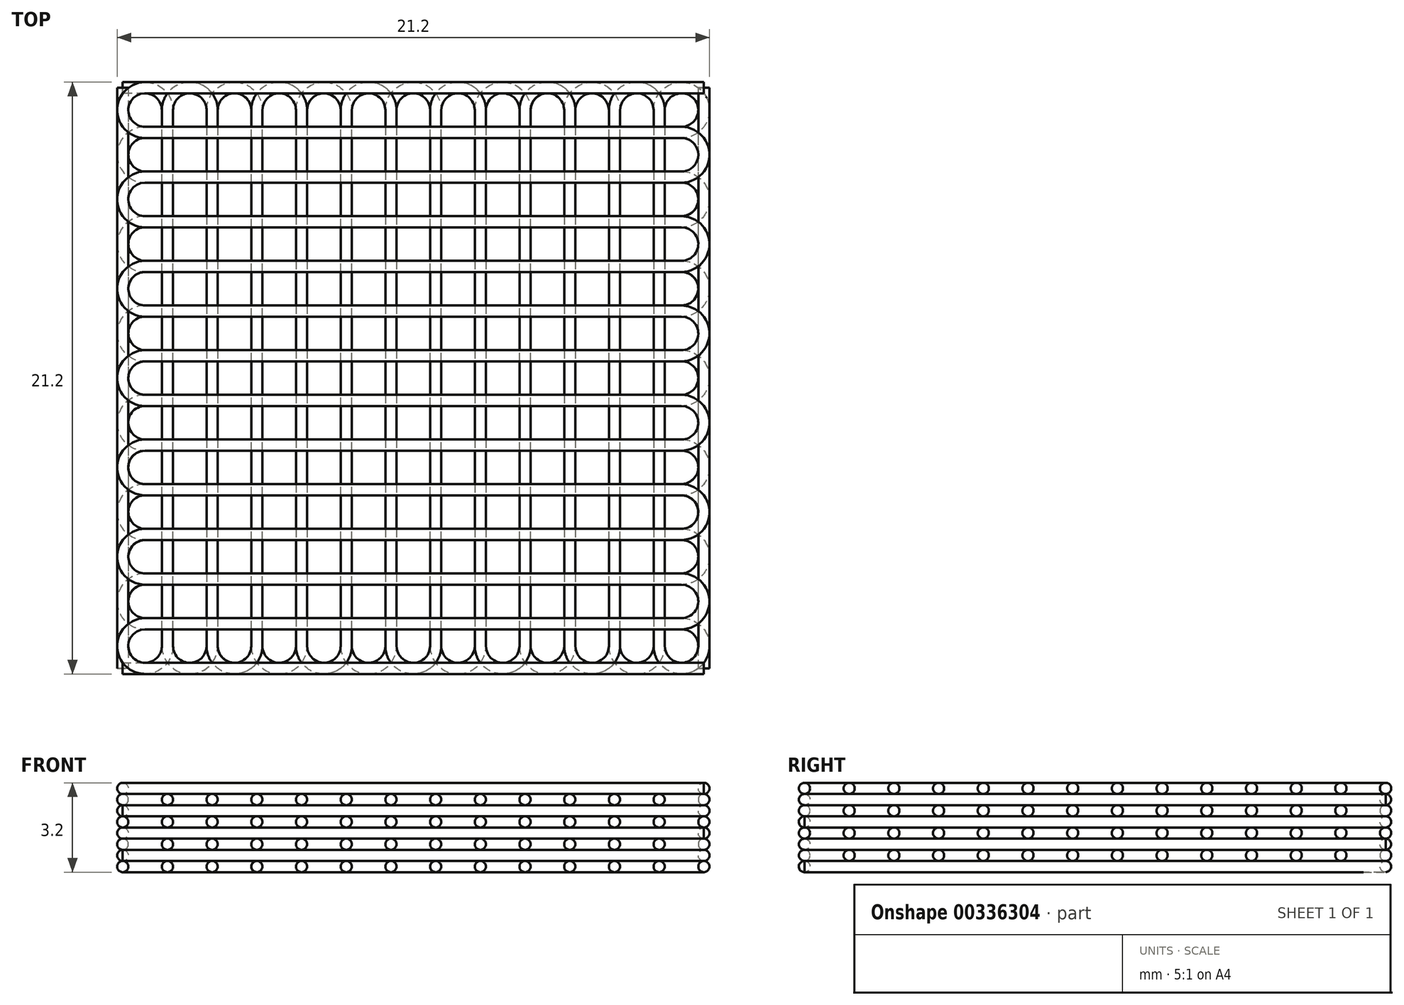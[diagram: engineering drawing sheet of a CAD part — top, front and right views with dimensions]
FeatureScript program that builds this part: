
annotation { "Feature Type Name" : "Feature", "Feature Type Description" : "" }
export const myFeature = defineFeature(function(context is Context, id is Id, definition is map)
    precondition{}
    {
        {
            var Q0;
            Q0=qCreatedBy(makeId("Top.planeOp"),FACE);
            cPlane(context, id + "F0", {"entities" : qUnion([Q0]), "cplaneType" : CPlaneType.OFFSET, "offset" : 0.2 * mm, "width" : 150 * mm, "height" : 150 * mm});
        }
        {
            var Q0;
            Q0=qCreatedBy(id+"F0.planeOp",FACE);
            var sketch = newSketch(context, id + "F1", { "sketchPlane" : qUnion([Q0])});
            skLineSegment(sketch, "E0.bottom", {"start": v(10.4, 10.4) * mm, "end": v(-10.4, 10.4) * mm});
            skLineSegment(sketch, "E0.top", {"start": v(10.4, -10.4) * mm, "end": v(-10.4, -10.4) * mm});
            skLineSegment(sketch, "E0.left", {"start": v(10.4, 9.6) * mm, "end": v(10.4, -10.4) * mm});
            skLineSegment(sketch, "E0.right", {"start": v(-10.4, 10.4) * mm, "end": v(-10.4, -10.4) * mm});
            skPoint(sketch, "E0.middle", {"position": v(0, 0) * mm});
            skLineSegment(sketch, "E1", {"start": v(7.2, 10.4) * mm, "end": v(7.2, -9.6) * mm});
            skLineSegment(sketch, "E2", {"start": v(8.8, -9.6) * mm, "end": v(8.8, 9.6) * mm});
            skLineSegment(sketch, "E3", {"start": v(10.4, 10.4) * mm, "end": v(10.4, -10.4) * mm});
            skArc(sketch, "E4", {"start": v(8.8, 9.6) * mm, "mid": v(9.6, 10.4) * mm, "end": v(10.4, 9.6) * mm});
            skArc(sketch, "E5", {"start": v(8.8, -9.6) * mm, "mid": v(8, -10.4) * mm, "end": v(7.2, -9.6) * mm});
            skLineSegment(sketch, "E6", {"start": v(7.2, -9.6) * mm, "end": v(7.2, 9.6) * mm});
            skLineSegment(sketch, "E7", {"start": v(10.4, 9.6) * mm, "end": v(10.4, -9.6) * mm});
            skLineSegment(sketch, "E8.1.0.0", {"start": v(7.2, 9.6) * mm, "end": v(7.2, -9.6) * mm});
            skArc(sketch, "E8.1.0.1", {"start": v(5.6, 9.6) * mm, "mid": v(6.4, 10.4) * mm, "end": v(7.2, 9.6) * mm});
            skLineSegment(sketch, "E8.1.0.2", {"start": v(5.6, -9.6) * mm, "end": v(5.6, 9.6) * mm});
            skArc(sketch, "E8.1.0.3", {"start": v(5.6, -9.6) * mm, "mid": v(4.8, -10.4) * mm, "end": v(4, -9.6) * mm});
            skLineSegment(sketch, "E8.1.0.4", {"start": v(4, -9.6) * mm, "end": v(4, 9.6) * mm});
            skLineSegment(sketch, "E8.2.0.0", {"start": v(4, 9.6) * mm, "end": v(4, -9.6) * mm});
            skArc(sketch, "E8.2.0.1", {"start": v(2.4, 9.6) * mm, "mid": v(3.2, 10.4) * mm, "end": v(4, 9.6) * mm});
            skLineSegment(sketch, "E8.2.0.2", {"start": v(2.4, -9.6) * mm, "end": v(2.4, 9.6) * mm});
            skArc(sketch, "E8.2.0.3", {"start": v(2.4, -9.6) * mm, "mid": v(1.6, -10.4) * mm, "end": v(0.8, -9.6) * mm});
            skLineSegment(sketch, "E8.2.0.4", {"start": v(0.8, -9.6) * mm, "end": v(0.8, 9.6) * mm});
            skLineSegment(sketch, "E8.3.0.0", {"start": v(0.8, 9.6) * mm, "end": v(0.8, -9.6) * mm});
            skArc(sketch, "E8.3.0.1", {"start": v(-0.8, 9.6) * mm, "mid": v(0, 10.4) * mm, "end": v(0.8, 9.6) * mm});
            skLineSegment(sketch, "E8.3.0.2", {"start": v(-0.8, -9.6) * mm, "end": v(-0.8, 9.6) * mm});
            skArc(sketch, "E8.3.0.3", {"start": v(-0.8, -9.6) * mm, "mid": v(-1.6, -10.4) * mm, "end": v(-2.4, -9.6) * mm});
            skLineSegment(sketch, "E8.3.0.4", {"start": v(-2.4, -9.6) * mm, "end": v(-2.4, 9.6) * mm});
            skLineSegment(sketch, "E8.4.0.0", {"start": v(-2.4, 9.6) * mm, "end": v(-2.4, -9.6) * mm});
            skArc(sketch, "E8.4.0.1", {"start": v(-4, 9.6) * mm, "mid": v(-3.2, 10.4) * mm, "end": v(-2.4, 9.6) * mm});
            skLineSegment(sketch, "E8.4.0.2", {"start": v(-4, -9.6) * mm, "end": v(-4, 9.6) * mm});
            skArc(sketch, "E8.4.0.3", {"start": v(-4, -9.6) * mm, "mid": v(-4.8, -10.4) * mm, "end": v(-5.6, -9.6) * mm});
            skLineSegment(sketch, "E8.4.0.4", {"start": v(-5.6, -9.6) * mm, "end": v(-5.6, 9.6) * mm});
            skLineSegment(sketch, "E8.5.0.0", {"start": v(-5.6, 9.6) * mm, "end": v(-5.6, -9.6) * mm});
            skArc(sketch, "E8.5.0.1", {"start": v(-7.2, 9.6) * mm, "mid": v(-6.4, 10.4) * mm, "end": v(-5.6, 9.6) * mm});
            skLineSegment(sketch, "E8.5.0.2", {"start": v(-7.2, -9.6) * mm, "end": v(-7.2, 9.6) * mm});
            skArc(sketch, "E8.5.0.3", {"start": v(-7.2, -9.6) * mm, "mid": v(-8, -10.4) * mm, "end": v(-8.8, -9.6) * mm});
            skLineSegment(sketch, "E8.5.0.4", {"start": v(-8.8, -9.6) * mm, "end": v(-8.8, 9.6) * mm});
            skLineSegment(sketch, "E8.direction1", {"start": v(7.2, -9.6) * mm, "end": v(4, -9.6) * mm, "construction": true});
            skArc(sketch, "E9", {"start": v(-8.8, 9.6) * mm, "mid": v(-9.6, 10.4) * mm, "end": v(-10.4, 9.6) * mm});
            skLineSegment(sketch, "E10", {"start": v(-10.4, 9.6) * mm, "end": v(-10.4, -10.4) * mm});
            skSolve(sketch);
        }
        {
            var Q0;
            Q0=sQuery(id+"F1.wireOp",EDGE,"E3");
            var Q1;
            Q1=sQuery(id+"F1.wireOp",VERTEX,"E0.left.end");
            cPlane(context, id + "F2", {"entities" : qUnion([Q0, Q1]), "cplaneType" : CPlaneType.LINE_POINT, "offset" : 25 * mm, "width" : 150 * mm, "height" : 150 * mm});
        }
        {
            var Q0;
            Q0=qCreatedBy(id+"F2.planeOp",FACE);
            var sketch = newSketch(context, id + "F3", { "sketchPlane" : qUnion([Q0])});
            skCircle(sketch, "E11", {"center": v(10.4, 0.2) * mm, "radius": 0.2 * mm});
            skSolve(sketch);
        }
        {
            var Q0;
            Q0=makeQuery(id+"F3.imprint","IMPRINT",FACE,{"disambiguationData":[TD([[makeQuery(id+"F3.imprint","IMPRINT",EDGE,{"derivedFrom":sQuery(id+"F3.wireOp",EDGE,"E11")}),1.0]])]});
            var Q1;
            Q1=sQuery(id+"F1.wireOp",EDGE,"E4");
            var Q2;
            Q2=sQuery(id+"F1.wireOp",EDGE,"E2");
            var Q3;
            Q3=sQuery(id+"F1.wireOp",EDGE,"E0.left");
            var Q4;
            Q4=sQuery(id+"F1.wireOp",EDGE,"E5");
            var Q5;
            Q5=sQuery(id+"F1.wireOp",EDGE,"E8.1.0.1");
            var Q6;
            Q6=sQuery(id+"F1.wireOp",EDGE,"E8.1.0.2");
            var Q7;
            Q7=sQuery(id+"F1.wireOp",EDGE,"E8.1.0.0");
            var Q8;
            Q8=sQuery(id+"F1.wireOp",EDGE,"E8.1.0.3");
            var Q9;
            Q9=sQuery(id+"F1.wireOp",EDGE,"E8.2.0.0");
            var Q10;
            Q10=sQuery(id+"F1.wireOp",EDGE,"E8.2.0.1");
            var Q11;
            Q11=sQuery(id+"F1.wireOp",EDGE,"E8.2.0.2");
            var Q12;
            Q12=sQuery(id+"F1.wireOp",EDGE,"E8.3.0.0");
            var Q13;
            Q13=sQuery(id+"F1.wireOp",EDGE,"E8.3.0.1");
            var Q14;
            Q14=sQuery(id+"F1.wireOp",EDGE,"E8.3.0.2");
            var Q15;
            Q15=sQuery(id+"F1.wireOp",EDGE,"E8.4.0.1");
            var Q16;
            Q16=sQuery(id+"F1.wireOp",EDGE,"E8.3.0.4");
            var Q17;
            Q17=sQuery(id+"F1.wireOp",EDGE,"E8.4.0.2");
            var Q18;
            Q18=sQuery(id+"F1.wireOp",EDGE,"E8.5.0.0");
            var Q19;
            Q19=sQuery(id+"F1.wireOp",EDGE,"E8.5.0.1");
            var Q20;
            Q20=sQuery(id+"F1.wireOp",EDGE,"E8.5.0.2");
            var Q21;
            Q21=sQuery(id+"F1.wireOp",EDGE,"E8.5.0.4");
            var Q22;
            Q22=sQuery(id+"F1.wireOp",EDGE,"E9");
            var Q23;
            Q23=sQuery(id+"F1.wireOp",EDGE,"E8.2.0.3");
            var Q24;
            Q24=sQuery(id+"F1.wireOp",EDGE,"E8.3.0.3");
            var Q25;
            Q25=sQuery(id+"F1.wireOp",EDGE,"E8.4.0.3");
            var Q26;
            Q26=sQuery(id+"F1.wireOp",EDGE,"E8.5.0.3");
            var Q27;
            Q27=sQuery(id+"F1.wireOp",EDGE,"E10");
            sweep(context, id + "F4", {"profiles" : qUnion([Q0]), "path" : qUnion([Q1, Q2, Q3, Q4, Q5, Q6, Q7, Q8, Q9, Q10, Q11, Q12, Q13, Q14, Q15, Q16, Q17, Q18, Q19, Q20, Q21, Q22, Q23, Q24, Q25, Q26, Q27])});
        }
        {
            var Q0;
            Q0=qCreatedBy(id+"F0.planeOp",FACE);
            cPlane(context, id + "F5", {"entities" : qUnion([Q0]), "cplaneType" : CPlaneType.OFFSET, "offset" : 0.4 * mm, "width" : 150 * mm, "height" : 150 * mm});
        }
        {
            var Q0;
            Q0=qCreatedBy(id+"F5.planeOp",FACE);
            var sketch = newSketch(context, id + "F6", { "sketchPlane" : qUnion([Q0])});
            skLineSegment(sketch, "E12.bottom", {"start": v(10.4, -10.4) * mm, "end": v(10.4, 10.4) * mm});
            skLineSegment(sketch, "E12.top", {"start": v(-10.4, -10.4) * mm, "end": v(-10.4, 10.4) * mm});
            skLineSegment(sketch, "E12.left", {"start": v(9.6, -10.4) * mm, "end": v(-10.4, -10.4) * mm});
            skLineSegment(sketch, "E12.right", {"start": v(10.4, 10.4) * mm, "end": v(-10.4, 10.4) * mm});
            skPoint(sketch, "E12.middle", {"position": v(0, 0) * mm});
            skLineSegment(sketch, "E13", {"start": v(10.4, -7.2) * mm, "end": v(-9.6, -7.2) * mm});
            skLineSegment(sketch, "E14", {"start": v(-9.6, -8.8) * mm, "end": v(9.6, -8.8) * mm});
            skLineSegment(sketch, "E15", {"start": v(10.4, -10.4) * mm, "end": v(-10.4, -10.4) * mm});
            skArc(sketch, "E16", {"start": v(9.6, -8.8) * mm, "mid": v(10.4, -9.6) * mm, "end": v(9.6, -10.4) * mm});
            skArc(sketch, "E17", {"start": v(-9.6, -8.8) * mm, "mid": v(-10.4, -8) * mm, "end": v(-9.6, -7.2) * mm});
            skLineSegment(sketch, "E18", {"start": v(-9.6, -7.2) * mm, "end": v(9.6, -7.2) * mm});
            skLineSegment(sketch, "E19", {"start": v(9.6, -10.4) * mm, "end": v(-9.6, -10.4) * mm});
            skLineSegment(sketch, "E20.1.0.0", {"start": v(9.6, -7.2) * mm, "end": v(-9.6, -7.2) * mm});
            skArc(sketch, "E20.1.0.1", {"start": v(9.6, -5.6) * mm, "mid": v(10.4, -6.4) * mm, "end": v(9.6, -7.2) * mm});
            skLineSegment(sketch, "E20.1.0.2", {"start": v(-9.6, -5.6) * mm, "end": v(9.6, -5.6) * mm});
            skArc(sketch, "E20.1.0.3", {"start": v(-9.6, -5.6) * mm, "mid": v(-10.4, -4.8) * mm, "end": v(-9.6, -4) * mm});
            skLineSegment(sketch, "E20.1.0.4", {"start": v(-9.6, -4) * mm, "end": v(9.6, -4) * mm});
            skLineSegment(sketch, "E20.2.0.0", {"start": v(9.6, -4) * mm, "end": v(-9.6, -4) * mm});
            skArc(sketch, "E20.2.0.1", {"start": v(9.6, -2.4) * mm, "mid": v(10.4, -3.2) * mm, "end": v(9.6, -4) * mm});
            skLineSegment(sketch, "E20.2.0.2", {"start": v(-9.6, -2.4) * mm, "end": v(9.6, -2.4) * mm});
            skArc(sketch, "E20.2.0.3", {"start": v(-9.6, -2.4) * mm, "mid": v(-10.4, -1.6) * mm, "end": v(-9.6, -0.8) * mm});
            skLineSegment(sketch, "E20.2.0.4", {"start": v(-9.6, -0.8) * mm, "end": v(9.6, -0.8) * mm});
            skLineSegment(sketch, "E20.3.0.0", {"start": v(9.6, -0.8) * mm, "end": v(-9.6, -0.8) * mm});
            skArc(sketch, "E20.3.0.1", {"start": v(9.6, 0.8) * mm, "mid": v(10.4, 0) * mm, "end": v(9.6, -0.8) * mm});
            skLineSegment(sketch, "E20.3.0.2", {"start": v(-9.6, 0.8) * mm, "end": v(9.6, 0.8) * mm});
            skArc(sketch, "E20.3.0.3", {"start": v(-9.6, 0.8) * mm, "mid": v(-10.4, 1.6) * mm, "end": v(-9.6, 2.4) * mm});
            skLineSegment(sketch, "E20.3.0.4", {"start": v(-9.6, 2.4) * mm, "end": v(9.6, 2.4) * mm});
            skLineSegment(sketch, "E20.4.0.0", {"start": v(9.6, 2.4) * mm, "end": v(-9.6, 2.4) * mm});
            skArc(sketch, "E20.4.0.1", {"start": v(9.6, 4) * mm, "mid": v(10.4, 3.2) * mm, "end": v(9.6, 2.4) * mm});
            skLineSegment(sketch, "E20.4.0.2", {"start": v(-9.6, 4) * mm, "end": v(9.6, 4) * mm});
            skArc(sketch, "E20.4.0.3", {"start": v(-9.6, 4) * mm, "mid": v(-10.4, 4.8) * mm, "end": v(-9.6, 5.6) * mm});
            skLineSegment(sketch, "E20.4.0.4", {"start": v(-9.6, 5.6) * mm, "end": v(9.6, 5.6) * mm});
            skLineSegment(sketch, "E20.5.0.0", {"start": v(9.6, 5.6) * mm, "end": v(-9.6, 5.6) * mm});
            skArc(sketch, "E20.5.0.1", {"start": v(9.6, 7.2) * mm, "mid": v(10.4, 6.4) * mm, "end": v(9.6, 5.6) * mm});
            skLineSegment(sketch, "E20.5.0.2", {"start": v(-9.6, 7.2) * mm, "end": v(9.6, 7.2) * mm});
            skArc(sketch, "E20.5.0.3", {"start": v(-9.6, 7.2) * mm, "mid": v(-10.4, 8) * mm, "end": v(-9.6, 8.8) * mm});
            skLineSegment(sketch, "E20.5.0.4", {"start": v(-9.6, 8.8) * mm, "end": v(9.6, 8.8) * mm});
            skLineSegment(sketch, "E20.direction1", {"start": v(-9.6, -7.2) * mm, "end": v(-9.6, -4) * mm, "construction": true});
            skArc(sketch, "E21", {"start": v(9.6, 8.8) * mm, "mid": v(10.4, 9.6) * mm, "end": v(9.6, 10.4) * mm});
            skLineSegment(sketch, "E22", {"start": v(9.6, 10.4) * mm, "end": v(-10.4, 10.4) * mm});
            skSolve(sketch);
        }
        {
            var Q0;
            Q0=sQuery(id+"F6.wireOp",EDGE,"E15");
            var Q1;
            Q1=sQuery(id+"F6.wireOp",VERTEX,"E12.left.end");
            cPlane(context, id + "F7", {"entities" : qUnion([Q0, Q1]), "cplaneType" : CPlaneType.LINE_POINT, "offset" : 25 * mm, "width" : 150 * mm, "height" : 150 * mm});
        }
        {
            var Q0;
            Q0=qCreatedBy(id+"F7.planeOp",FACE);
            var sketch = newSketch(context, id + "F8", { "sketchPlane" : qUnion([Q0])});
            skCircle(sketch, "E23", {"center": v(10.4, 0.6) * mm, "radius": 0.2 * mm});
            skSolve(sketch);
        }
        {
            var Q0;
            Q0=makeQuery(id+"F8.imprint","IMPRINT",FACE,{"disambiguationData":[TD([[makeQuery(id+"F8.imprint","IMPRINT",EDGE,{"derivedFrom":sQuery(id+"F8.wireOp",EDGE,"E23")}),1.0]])]});
            var Q1;
            Q1=sQuery(id+"F6.wireOp",EDGE,"E12.left");
            var Q2;
            Q2=sQuery(id+"F6.wireOp",EDGE,"E16");
            var Q3;
            Q3=sQuery(id+"F6.wireOp",EDGE,"E14");
            var Q4;
            Q4=sQuery(id+"F6.wireOp",EDGE,"E17");
            var Q5;
            Q5=sQuery(id+"F6.wireOp",EDGE,"E20.1.0.0");
            var Q6;
            Q6=sQuery(id+"F6.wireOp",EDGE,"E20.1.0.1");
            var Q7;
            Q7=sQuery(id+"F6.wireOp",EDGE,"E20.1.0.2");
            var Q8;
            Q8=sQuery(id+"F6.wireOp",EDGE,"E20.1.0.3");
            var Q9;
            Q9=sQuery(id+"F6.wireOp",EDGE,"E20.1.0.4");
            var Q10;
            Q10=sQuery(id+"F6.wireOp",EDGE,"E20.2.0.1");
            var Q11;
            Q11=sQuery(id+"F6.wireOp",EDGE,"E20.2.0.2");
            var Q12;
            Q12=sQuery(id+"F6.wireOp",EDGE,"E20.2.0.3");
            var Q13;
            Q13=sQuery(id+"F6.wireOp",EDGE,"E20.3.0.0");
            var Q14;
            Q14=sQuery(id+"F6.wireOp",EDGE,"E20.3.0.1");
            var Q15;
            Q15=sQuery(id+"F6.wireOp",EDGE,"E20.3.0.2");
            var Q16;
            Q16=sQuery(id+"F6.wireOp",EDGE,"E20.3.0.3");
            var Q17;
            Q17=sQuery(id+"F6.wireOp",EDGE,"E20.3.0.4");
            var Q18;
            Q18=sQuery(id+"F6.wireOp",EDGE,"E20.4.0.2");
            var Q19;
            Q19=sQuery(id+"F6.wireOp",EDGE,"E20.4.0.3");
            var Q20;
            Q20=sQuery(id+"F6.wireOp",EDGE,"E20.5.0.0");
            var Q21;
            Q21=sQuery(id+"F6.wireOp",EDGE,"E20.5.0.2");
            var Q22;
            Q22=sQuery(id+"F6.wireOp",EDGE,"E20.5.0.3");
            var Q23;
            Q23=sQuery(id+"F6.wireOp",EDGE,"E20.5.0.4");
            var Q24;
            Q24=sQuery(id+"F6.wireOp",EDGE,"E22");
            var Q25;
            Q25=sQuery(id+"F6.wireOp",EDGE,"E21");
            var Q26;
            Q26=sQuery(id+"F6.wireOp",EDGE,"E20.5.0.1");
            var Q27;
            Q27=sQuery(id+"F6.wireOp",EDGE,"E20.4.0.1");
            sweep(context, id + "F9", {"operationType" : NewBodyOperationType.ADD, "profiles" : qUnion([Q0]), "path" : qUnion([Q1, Q2, Q3, Q4, Q5, Q6, Q7, Q8, Q9, Q10, Q11, Q12, Q13, Q14, Q15, Q16, Q17, Q18, Q19, Q20, Q21, Q22, Q23, Q24, Q25, Q26, Q27])});
        }
        {
            var Q0;
            Q0=qCreatedBy(id+"F5.planeOp",FACE);
            cPlane(context, id + "F10", {"entities" : qUnion([Q0]), "cplaneType" : CPlaneType.OFFSET, "offset" : 0.4 * mm, "width" : 150 * mm, "height" : 150 * mm});
        }
        {
            var Q0;
            Q0=qCreatedBy(id+"F10.planeOp",FACE);
            var sketch = newSketch(context, id + "F11", { "sketchPlane" : qUnion([Q0])});
            skLineSegment(sketch, "E24.bottom", {"start": v(-10.4, -10.4) * mm, "end": v(10.4, -10.4) * mm});
            skLineSegment(sketch, "E24.top", {"start": v(-10.4, 10.4) * mm, "end": v(10.4, 10.4) * mm});
            skLineSegment(sketch, "E24.left", {"start": v(-10.4, -9.6) * mm, "end": v(-10.4, 10.4) * mm});
            skLineSegment(sketch, "E24.right", {"start": v(10.4, -10.4) * mm, "end": v(10.4, 10.4) * mm});
            skPoint(sketch, "E24.middle", {"position": v(0, 0) * mm});
            skLineSegment(sketch, "E25", {"start": v(-7.2, -10.4) * mm, "end": v(-7.2, 9.6) * mm});
            skLineSegment(sketch, "E26", {"start": v(-8.8, 9.6) * mm, "end": v(-8.8, -9.6) * mm});
            skLineSegment(sketch, "E27", {"start": v(-10.4, -10.4) * mm, "end": v(-10.4, 10.4) * mm});
            skArc(sketch, "E28", {"start": v(-8.8, -9.6) * mm, "mid": v(-9.6, -10.4) * mm, "end": v(-10.4, -9.6) * mm});
            skArc(sketch, "E29", {"start": v(-8.8, 9.6) * mm, "mid": v(-8, 10.4) * mm, "end": v(-7.2, 9.6) * mm});
            skLineSegment(sketch, "E30", {"start": v(-7.2, 9.6) * mm, "end": v(-7.2, -9.6) * mm});
            skLineSegment(sketch, "E31", {"start": v(-10.4, -9.6) * mm, "end": v(-10.4, 9.6) * mm});
            skLineSegment(sketch, "E32.1.0.0", {"start": v(-7.2, -9.6) * mm, "end": v(-7.2, 9.6) * mm});
            skArc(sketch, "E32.1.0.1", {"start": v(-5.6, -9.6) * mm, "mid": v(-6.4, -10.4) * mm, "end": v(-7.2, -9.6) * mm});
            skLineSegment(sketch, "E32.1.0.2", {"start": v(-5.6, 9.6) * mm, "end": v(-5.6, -9.6) * mm});
            skArc(sketch, "E32.1.0.3", {"start": v(-5.6, 9.6) * mm, "mid": v(-4.8, 10.4) * mm, "end": v(-4, 9.6) * mm});
            skLineSegment(sketch, "E32.1.0.4", {"start": v(-4, 9.6) * mm, "end": v(-4, -9.6) * mm});
            skLineSegment(sketch, "E32.2.0.0", {"start": v(-4, -9.6) * mm, "end": v(-4, 9.6) * mm});
            skArc(sketch, "E32.2.0.1", {"start": v(-2.4, -9.6) * mm, "mid": v(-3.2, -10.4) * mm, "end": v(-4, -9.6) * mm});
            skLineSegment(sketch, "E32.2.0.2", {"start": v(-2.4, 9.6) * mm, "end": v(-2.4, -9.6) * mm});
            skArc(sketch, "E32.2.0.3", {"start": v(-2.4, 9.6) * mm, "mid": v(-1.6, 10.4) * mm, "end": v(-0.8, 9.6) * mm});
            skLineSegment(sketch, "E32.2.0.4", {"start": v(-0.8, 9.6) * mm, "end": v(-0.8, -9.6) * mm});
            skLineSegment(sketch, "E32.3.0.0", {"start": v(-0.8, -9.6) * mm, "end": v(-0.8, 9.6) * mm});
            skArc(sketch, "E32.3.0.1", {"start": v(0.8, -9.6) * mm, "mid": v(0, -10.4) * mm, "end": v(-0.8, -9.6) * mm});
            skLineSegment(sketch, "E32.3.0.2", {"start": v(0.8, 9.6) * mm, "end": v(0.8, -9.6) * mm});
            skArc(sketch, "E32.3.0.3", {"start": v(0.8, 9.6) * mm, "mid": v(1.6, 10.4) * mm, "end": v(2.4, 9.6) * mm});
            skLineSegment(sketch, "E32.3.0.4", {"start": v(2.4, 9.6) * mm, "end": v(2.4, -9.6) * mm});
            skLineSegment(sketch, "E32.4.0.0", {"start": v(2.4, -9.6) * mm, "end": v(2.4, 9.6) * mm});
            skArc(sketch, "E32.4.0.1", {"start": v(4, -9.6) * mm, "mid": v(3.2, -10.4) * mm, "end": v(2.4, -9.6) * mm});
            skLineSegment(sketch, "E32.4.0.2", {"start": v(4, 9.6) * mm, "end": v(4, -9.6) * mm});
            skArc(sketch, "E32.4.0.3", {"start": v(4, 9.6) * mm, "mid": v(4.8, 10.4) * mm, "end": v(5.6, 9.6) * mm});
            skLineSegment(sketch, "E32.4.0.4", {"start": v(5.6, 9.6) * mm, "end": v(5.6, -9.6) * mm});
            skLineSegment(sketch, "E32.5.0.0", {"start": v(5.6, -9.6) * mm, "end": v(5.6, 9.6) * mm});
            skArc(sketch, "E32.5.0.1", {"start": v(7.2, -9.6) * mm, "mid": v(6.4, -10.4) * mm, "end": v(5.6, -9.6) * mm});
            skLineSegment(sketch, "E32.5.0.2", {"start": v(7.2, 9.6) * mm, "end": v(7.2, -9.6) * mm});
            skArc(sketch, "E32.5.0.3", {"start": v(7.2, 9.6) * mm, "mid": v(8, 10.4) * mm, "end": v(8.8, 9.6) * mm});
            skLineSegment(sketch, "E32.5.0.4", {"start": v(8.8, 9.6) * mm, "end": v(8.8, -9.6) * mm});
            skLineSegment(sketch, "E32.direction1", {"start": v(-7.2, 9.6) * mm, "end": v(-4, 9.6) * mm, "construction": true});
            skArc(sketch, "E33", {"start": v(8.8, -9.6) * mm, "mid": v(9.6, -10.4) * mm, "end": v(10.4, -9.6) * mm});
            skLineSegment(sketch, "E34", {"start": v(10.4, -9.6) * mm, "end": v(10.4, 10.4) * mm});
            skSolve(sketch);
        }
        {
            var Q0;
            Q0=sQuery(id+"F11.wireOp",EDGE,"E27");
            var Q1;
            Q1=sQuery(id+"F11.wireOp",VERTEX,"E24.left.end");
            cPlane(context, id + "F12", {"entities" : qUnion([Q0, Q1]), "cplaneType" : CPlaneType.LINE_POINT, "offset" : 25 * mm, "width" : 150 * mm, "height" : 150 * mm});
        }
        {
            var Q0;
            Q0=qCreatedBy(id+"F12.planeOp",FACE);
            var sketch = newSketch(context, id + "F13", { "sketchPlane" : qUnion([Q0])});
            skCircle(sketch, "E35", {"center": v(10.4, 1) * mm, "radius": 0.2 * mm});
            skSolve(sketch);
        }
        {
            var Q0;
            Q0=makeQuery(id+"F13.imprint","IMPRINT",FACE,{"disambiguationData":[TD([[makeQuery(id+"F13.imprint","IMPRINT",EDGE,{"derivedFrom":sQuery(id+"F13.wireOp",EDGE,"E35")}),1.0]])]});
            var Q1;
            Q1=sQuery(id+"F11.wireOp",EDGE,"E24.left");
            var Q2;
            Q2=sQuery(id+"F11.wireOp",EDGE,"E28");
            var Q3;
            Q3=sQuery(id+"F11.wireOp",EDGE,"E26");
            var Q4;
            Q4=sQuery(id+"F11.wireOp",EDGE,"E29");
            var Q5;
            Q5=sQuery(id+"F11.wireOp",EDGE,"E32.1.0.0");
            var Q6;
            Q6=sQuery(id+"F11.wireOp",EDGE,"E32.1.0.1");
            var Q7;
            Q7=sQuery(id+"F11.wireOp",EDGE,"E32.1.0.2");
            var Q8;
            Q8=sQuery(id+"F11.wireOp",EDGE,"E32.1.0.3");
            var Q9;
            Q9=sQuery(id+"F11.wireOp",EDGE,"E32.2.0.0");
            var Q10;
            Q10=sQuery(id+"F11.wireOp",EDGE,"E32.2.0.1");
            var Q11;
            Q11=sQuery(id+"F11.wireOp",EDGE,"E32.2.0.2");
            var Q12;
            Q12=sQuery(id+"F11.wireOp",EDGE,"E32.2.0.3");
            var Q13;
            Q13=sQuery(id+"F11.wireOp",EDGE,"E32.3.0.0");
            var Q14;
            Q14=sQuery(id+"F11.wireOp",EDGE,"E32.3.0.1");
            var Q15;
            Q15=sQuery(id+"F11.wireOp",EDGE,"E32.3.0.2");
            var Q16;
            Q16=sQuery(id+"F11.wireOp",EDGE,"E32.3.0.3");
            var Q17;
            Q17=sQuery(id+"F11.wireOp",EDGE,"E32.3.0.4");
            var Q18;
            Q18=sQuery(id+"F11.wireOp",EDGE,"E32.4.0.1");
            var Q19;
            Q19=sQuery(id+"F11.wireOp",EDGE,"E32.4.0.2");
            var Q20;
            Q20=sQuery(id+"F11.wireOp",EDGE,"E32.4.0.3");
            var Q21;
            Q21=sQuery(id+"F11.wireOp",EDGE,"E32.5.0.0");
            var Q22;
            Q22=sQuery(id+"F11.wireOp",EDGE,"E32.5.0.1");
            var Q23;
            Q23=sQuery(id+"F11.wireOp",EDGE,"E32.5.0.2");
            var Q24;
            Q24=sQuery(id+"F11.wireOp",EDGE,"E32.5.0.3");
            var Q25;
            Q25=sQuery(id+"F11.wireOp",EDGE,"E32.5.0.4");
            var Q26;
            Q26=sQuery(id+"F11.wireOp",EDGE,"E33");
            var Q27;
            Q27=sQuery(id+"F11.wireOp",EDGE,"E34");
            sweep(context, id + "F14", {"operationType" : NewBodyOperationType.ADD, "profiles" : qUnion([Q0]), "path" : qUnion([Q1, Q2, Q3, Q4, Q5, Q6, Q7, Q8, Q9, Q10, Q11, Q12, Q13, Q14, Q15, Q16, Q17, Q18, Q19, Q20, Q21, Q22, Q23, Q24, Q25, Q26, Q27])});
        }
        {
            var Q0;
            Q0=qCreatedBy(id+"F10.planeOp",FACE);
            cPlane(context, id + "F15", {"entities" : qUnion([Q0]), "cplaneType" : CPlaneType.OFFSET, "offset" : 0.4 * mm, "width" : 150 * mm, "height" : 150 * mm});
        }
        {
            var Q0;
            Q0=qCreatedBy(id+"F15.planeOp",FACE);
            var sketch = newSketch(context, id + "F16", { "sketchPlane" : qUnion([Q0])});
            skLineSegment(sketch, "E36.bottom", {"start": v(-10.4, 10.4) * mm, "end": v(-10.4, -10.4) * mm});
            skLineSegment(sketch, "E36.top", {"start": v(10.4, 10.4) * mm, "end": v(10.4, -10.4) * mm});
            skLineSegment(sketch, "E36.left", {"start": v(-9.6, 10.4) * mm, "end": v(10.4, 10.4) * mm});
            skLineSegment(sketch, "E36.right", {"start": v(-10.4, -10.4) * mm, "end": v(10.4, -10.4) * mm});
            skPoint(sketch, "E36.middle", {"position": v(0, 0) * mm});
            skLineSegment(sketch, "E37", {"start": v(-10.4, 7.2) * mm, "end": v(9.6, 7.2) * mm});
            skLineSegment(sketch, "E38", {"start": v(9.6, 8.8) * mm, "end": v(-9.6, 8.8) * mm});
            skLineSegment(sketch, "E39", {"start": v(-10.4, 10.4) * mm, "end": v(10.4, 10.4) * mm});
            skArc(sketch, "E40", {"start": v(-9.6, 8.8) * mm, "mid": v(-10.4, 9.6) * mm, "end": v(-9.6, 10.4) * mm});
            skArc(sketch, "E41", {"start": v(9.6, 8.8) * mm, "mid": v(10.4, 8) * mm, "end": v(9.6, 7.2) * mm});
            skLineSegment(sketch, "E42", {"start": v(9.6, 7.2) * mm, "end": v(-9.6, 7.2) * mm});
            skLineSegment(sketch, "E43", {"start": v(-9.6, 10.4) * mm, "end": v(9.6, 10.4) * mm});
            skLineSegment(sketch, "E44.1.0.0", {"start": v(-9.6, 7.2) * mm, "end": v(9.6, 7.2) * mm});
            skArc(sketch, "E44.1.0.1", {"start": v(-9.6, 5.6) * mm, "mid": v(-10.4, 6.4) * mm, "end": v(-9.6, 7.2) * mm});
            skLineSegment(sketch, "E44.1.0.2", {"start": v(9.6, 5.6) * mm, "end": v(-9.6, 5.6) * mm});
            skArc(sketch, "E44.1.0.3", {"start": v(9.6, 5.6) * mm, "mid": v(10.4, 4.8) * mm, "end": v(9.6, 4) * mm});
            skLineSegment(sketch, "E44.1.0.4", {"start": v(9.6, 4) * mm, "end": v(-9.6, 4) * mm});
            skLineSegment(sketch, "E44.2.0.0", {"start": v(-9.6, 4) * mm, "end": v(9.6, 4) * mm});
            skArc(sketch, "E44.2.0.1", {"start": v(-9.6, 2.4) * mm, "mid": v(-10.4, 3.2) * mm, "end": v(-9.6, 4) * mm});
            skLineSegment(sketch, "E44.2.0.2", {"start": v(9.6, 2.4) * mm, "end": v(-9.6, 2.4) * mm});
            skArc(sketch, "E44.2.0.3", {"start": v(9.6, 2.4) * mm, "mid": v(10.4, 1.6) * mm, "end": v(9.6, 0.8) * mm});
            skLineSegment(sketch, "E44.2.0.4", {"start": v(9.6, 0.8) * mm, "end": v(-9.6, 0.8) * mm});
            skLineSegment(sketch, "E44.3.0.0", {"start": v(-9.6, 0.8) * mm, "end": v(9.6, 0.8) * mm});
            skArc(sketch, "E44.3.0.1", {"start": v(-9.6, -0.8) * mm, "mid": v(-10.4, 0) * mm, "end": v(-9.6, 0.8) * mm});
            skLineSegment(sketch, "E44.3.0.2", {"start": v(9.6, -0.8) * mm, "end": v(-9.6, -0.8) * mm});
            skArc(sketch, "E44.3.0.3", {"start": v(9.6, -0.8) * mm, "mid": v(10.4, -1.6) * mm, "end": v(9.6, -2.4) * mm});
            skLineSegment(sketch, "E44.3.0.4", {"start": v(9.6, -2.4) * mm, "end": v(-9.6, -2.4) * mm});
            skLineSegment(sketch, "E44.4.0.0", {"start": v(-9.6, -2.4) * mm, "end": v(9.6, -2.4) * mm});
            skArc(sketch, "E44.4.0.1", {"start": v(-9.6, -4) * mm, "mid": v(-10.4, -3.2) * mm, "end": v(-9.6, -2.4) * mm});
            skLineSegment(sketch, "E44.4.0.2", {"start": v(9.6, -4) * mm, "end": v(-9.6, -4) * mm});
            skArc(sketch, "E44.4.0.3", {"start": v(9.6, -4) * mm, "mid": v(10.4, -4.8) * mm, "end": v(9.6, -5.6) * mm});
            skLineSegment(sketch, "E44.4.0.4", {"start": v(9.6, -5.6) * mm, "end": v(-9.6, -5.6) * mm});
            skLineSegment(sketch, "E44.5.0.0", {"start": v(-9.6, -5.6) * mm, "end": v(9.6, -5.6) * mm});
            skArc(sketch, "E44.5.0.1", {"start": v(-9.6, -7.2) * mm, "mid": v(-10.4, -6.4) * mm, "end": v(-9.6, -5.6) * mm});
            skLineSegment(sketch, "E44.5.0.2", {"start": v(9.6, -7.2) * mm, "end": v(-9.6, -7.2) * mm});
            skArc(sketch, "E44.5.0.3", {"start": v(9.6, -7.2) * mm, "mid": v(10.4, -8) * mm, "end": v(9.6, -8.8) * mm});
            skLineSegment(sketch, "E44.5.0.4", {"start": v(9.6, -8.8) * mm, "end": v(-9.6, -8.8) * mm});
            skLineSegment(sketch, "E44.direction1", {"start": v(9.6, 7.2) * mm, "end": v(9.6, 4) * mm, "construction": true});
            skArc(sketch, "E45", {"start": v(-9.6, -8.8) * mm, "mid": v(-10.4, -9.6) * mm, "end": v(-9.6, -10.4) * mm});
            skLineSegment(sketch, "E46", {"start": v(-9.6, -10.4) * mm, "end": v(10.4, -10.4) * mm});
            skSolve(sketch);
        }
        {
            var Q0;
            Q0=sQuery(id+"F16.wireOp",EDGE,"E39");
            var Q1;
            Q1=sQuery(id+"F16.wireOp",VERTEX,"E36.left.end");
            cPlane(context, id + "F17", {"entities" : qUnion([Q0, Q1]), "cplaneType" : CPlaneType.LINE_POINT, "offset" : 25 * mm, "width" : 150 * mm, "height" : 150 * mm});
        }
        {
            var Q0;
            Q0=qCreatedBy(id+"F17.planeOp",FACE);
            var sketch = newSketch(context, id + "F18", { "sketchPlane" : qUnion([Q0])});
            skCircle(sketch, "E47", {"center": v(10.4, 1.4) * mm, "radius": 0.2 * mm});
            skSolve(sketch);
        }
        {
            var Q0;
            Q0=makeQuery(id+"F18.imprint","IMPRINT",FACE,{"disambiguationData":[TD([[makeQuery(id+"F18.imprint","IMPRINT",EDGE,{"derivedFrom":sQuery(id+"F18.wireOp",EDGE,"E47")}),1.0]])]});
            var Q1;
            Q1=sQuery(id+"F16.wireOp",EDGE,"E36.left");
            var Q2;
            Q2=sQuery(id+"F16.wireOp",EDGE,"E40");
            var Q3;
            Q3=sQuery(id+"F16.wireOp",EDGE,"E38");
            var Q4;
            Q4=sQuery(id+"F16.wireOp",EDGE,"E44.1.0.0");
            var Q5;
            Q5=sQuery(id+"F16.wireOp",EDGE,"E44.1.0.1");
            var Q6;
            Q6=sQuery(id+"F16.wireOp",EDGE,"E44.1.0.2");
            var Q7;
            Q7=sQuery(id+"F16.wireOp",EDGE,"E44.2.0.0");
            var Q8;
            Q8=sQuery(id+"F16.wireOp",EDGE,"E44.2.0.1");
            var Q9;
            Q9=sQuery(id+"F16.wireOp",EDGE,"E44.2.0.2");
            var Q10;
            Q10=sQuery(id+"F16.wireOp",EDGE,"E44.3.0.0");
            var Q11;
            Q11=sQuery(id+"F16.wireOp",EDGE,"E44.3.0.1");
            var Q12;
            Q12=sQuery(id+"F16.wireOp",EDGE,"E44.3.0.2");
            var Q13;
            Q13=sQuery(id+"F16.wireOp",EDGE,"E44.4.0.0");
            var Q14;
            Q14=sQuery(id+"F16.wireOp",EDGE,"E44.4.0.1");
            var Q15;
            Q15=sQuery(id+"F16.wireOp",EDGE,"E44.4.0.2");
            var Q16;
            Q16=sQuery(id+"F16.wireOp",EDGE,"E44.5.0.0");
            var Q17;
            Q17=sQuery(id+"F16.wireOp",EDGE,"E44.5.0.1");
            var Q18;
            Q18=sQuery(id+"F16.wireOp",EDGE,"E44.5.0.2");
            var Q19;
            Q19=sQuery(id+"F16.wireOp",EDGE,"E44.5.0.4");
            var Q20;
            Q20=sQuery(id+"F16.wireOp",EDGE,"E45");
            var Q21;
            Q21=sQuery(id+"F16.wireOp",EDGE,"E44.5.0.3");
            var Q22;
            Q22=sQuery(id+"F16.wireOp",EDGE,"E44.4.0.3");
            var Q23;
            Q23=sQuery(id+"F16.wireOp",EDGE,"E44.3.0.3");
            var Q24;
            Q24=sQuery(id+"F16.wireOp",EDGE,"E44.1.0.3");
            var Q25;
            Q25=sQuery(id+"F16.wireOp",EDGE,"E44.2.0.3");
            var Q26;
            Q26=sQuery(id+"F16.wireOp",EDGE,"E41");
            var Q27;
            Q27=sQuery(id+"F16.wireOp",EDGE,"E46");
            sweep(context, id + "F19", {"operationType" : NewBodyOperationType.ADD, "profiles" : qUnion([Q0]), "path" : qUnion([Q1, Q2, Q3, Q4, Q5, Q6, Q7, Q8, Q9, Q10, Q11, Q12, Q13, Q14, Q15, Q16, Q17, Q18, Q19, Q20, Q21, Q22, Q23, Q24, Q25, Q26, Q27])});
        }
        {
            var Q0;
            Q0=qCreatedBy(id+"F15.planeOp",FACE);
            cPlane(context, id + "F20", {"entities" : qUnion([Q0]), "cplaneType" : CPlaneType.OFFSET, "offset" : 0.4 * mm, "width" : 150 * mm, "height" : 150 * mm});
        }
        {
            var Q0;
            Q0=qCreatedBy(id+"F20.planeOp",FACE);
            var sketch = newSketch(context, id + "F21", { "sketchPlane" : qUnion([Q0])});
            skLineSegment(sketch, "E48.bottom", {"start": v(10.4, 10.4) * mm, "end": v(-10.4, 10.4) * mm});
            skLineSegment(sketch, "E48.top", {"start": v(10.4, -10.4) * mm, "end": v(-10.4, -10.4) * mm});
            skLineSegment(sketch, "E48.left", {"start": v(10.4, 9.6) * mm, "end": v(10.4, -10.4) * mm});
            skLineSegment(sketch, "E48.right", {"start": v(-10.4, 10.4) * mm, "end": v(-10.4, -10.4) * mm});
            skPoint(sketch, "E48.middle", {"position": v(0, 0) * mm});
            skLineSegment(sketch, "E49", {"start": v(7.2, 10.4) * mm, "end": v(7.2, -9.6) * mm});
            skLineSegment(sketch, "E50", {"start": v(8.8, -9.6) * mm, "end": v(8.8, 9.6) * mm});
            skLineSegment(sketch, "E51", {"start": v(10.4, 10.4) * mm, "end": v(10.4, -10.4) * mm});
            skArc(sketch, "E52", {"start": v(8.8, 9.6) * mm, "mid": v(9.6, 10.4) * mm, "end": v(10.4, 9.6) * mm});
            skArc(sketch, "E53", {"start": v(8.8, -9.6) * mm, "mid": v(8, -10.4) * mm, "end": v(7.2, -9.6) * mm});
            skLineSegment(sketch, "E54", {"start": v(7.2, -9.6) * mm, "end": v(7.2, 9.6) * mm});
            skLineSegment(sketch, "E55", {"start": v(10.4, 9.6) * mm, "end": v(10.4, -9.6) * mm});
            skLineSegment(sketch, "E56.1.0.0", {"start": v(7.2, 9.6) * mm, "end": v(7.2, -9.6) * mm});
            skArc(sketch, "E56.1.0.1", {"start": v(5.6, 9.6) * mm, "mid": v(6.4, 10.4) * mm, "end": v(7.2, 9.6) * mm});
            skLineSegment(sketch, "E56.1.0.2", {"start": v(5.6, -9.6) * mm, "end": v(5.6, 9.6) * mm});
            skArc(sketch, "E56.1.0.3", {"start": v(5.6, -9.6) * mm, "mid": v(4.8, -10.4) * mm, "end": v(4, -9.6) * mm});
            skLineSegment(sketch, "E56.1.0.4", {"start": v(4, -9.6) * mm, "end": v(4, 9.6) * mm});
            skLineSegment(sketch, "E56.2.0.0", {"start": v(4, 9.6) * mm, "end": v(4, -9.6) * mm});
            skArc(sketch, "E56.2.0.1", {"start": v(2.4, 9.6) * mm, "mid": v(3.2, 10.4) * mm, "end": v(4, 9.6) * mm});
            skLineSegment(sketch, "E56.2.0.2", {"start": v(2.4, -9.6) * mm, "end": v(2.4, 9.6) * mm});
            skArc(sketch, "E56.2.0.3", {"start": v(2.4, -9.6) * mm, "mid": v(1.6, -10.4) * mm, "end": v(0.8, -9.6) * mm});
            skLineSegment(sketch, "E56.2.0.4", {"start": v(0.8, -9.6) * mm, "end": v(0.8, 9.6) * mm});
            skLineSegment(sketch, "E56.3.0.0", {"start": v(0.8, 9.6) * mm, "end": v(0.8, -9.6) * mm});
            skArc(sketch, "E56.3.0.1", {"start": v(-0.8, 9.6) * mm, "mid": v(0, 10.4) * mm, "end": v(0.8, 9.6) * mm});
            skLineSegment(sketch, "E56.3.0.2", {"start": v(-0.8, -9.6) * mm, "end": v(-0.8, 9.6) * mm});
            skArc(sketch, "E56.3.0.3", {"start": v(-0.8, -9.6) * mm, "mid": v(-1.6, -10.4) * mm, "end": v(-2.4, -9.6) * mm});
            skLineSegment(sketch, "E56.3.0.4", {"start": v(-2.4, -9.6) * mm, "end": v(-2.4, 9.6) * mm});
            skLineSegment(sketch, "E56.4.0.0", {"start": v(-2.4, 9.6) * mm, "end": v(-2.4, -9.6) * mm});
            skArc(sketch, "E56.4.0.1", {"start": v(-4, 9.6) * mm, "mid": v(-3.2, 10.4) * mm, "end": v(-2.4, 9.6) * mm});
            skLineSegment(sketch, "E56.4.0.2", {"start": v(-4, -9.6) * mm, "end": v(-4, 9.6) * mm});
            skArc(sketch, "E56.4.0.3", {"start": v(-4, -9.6) * mm, "mid": v(-4.8, -10.4) * mm, "end": v(-5.6, -9.6) * mm});
            skLineSegment(sketch, "E56.4.0.4", {"start": v(-5.6, -9.6) * mm, "end": v(-5.6, 9.6) * mm});
            skLineSegment(sketch, "E56.5.0.0", {"start": v(-5.6, 9.6) * mm, "end": v(-5.6, -9.6) * mm});
            skArc(sketch, "E56.5.0.1", {"start": v(-7.2, 9.6) * mm, "mid": v(-6.4, 10.4) * mm, "end": v(-5.6, 9.6) * mm});
            skLineSegment(sketch, "E56.5.0.2", {"start": v(-7.2, -9.6) * mm, "end": v(-7.2, 9.6) * mm});
            skArc(sketch, "E56.5.0.3", {"start": v(-7.2, -9.6) * mm, "mid": v(-8, -10.4) * mm, "end": v(-8.8, -9.6) * mm});
            skLineSegment(sketch, "E56.5.0.4", {"start": v(-8.8, -9.6) * mm, "end": v(-8.8, 9.6) * mm});
            skLineSegment(sketch, "E56.direction1", {"start": v(7.2, -9.6) * mm, "end": v(4, -9.6) * mm, "construction": true});
            skArc(sketch, "E57", {"start": v(-8.8, 9.6) * mm, "mid": v(-9.6, 10.4) * mm, "end": v(-10.4, 9.6) * mm});
            skLineSegment(sketch, "E58", {"start": v(-10.4, 9.6) * mm, "end": v(-10.4, -10.4) * mm});
            skSolve(sketch);
        }
        {
            var Q0;
            Q0=sQuery(id+"F21.wireOp",EDGE,"E51");
            var Q1;
            Q1=sQuery(id+"F21.wireOp",VERTEX,"E48.left.end");
            cPlane(context, id + "F22", {"entities" : qUnion([Q0, Q1]), "cplaneType" : CPlaneType.LINE_POINT, "offset" : 25 * mm, "width" : 150 * mm, "height" : 150 * mm});
        }
        {
            var Q0;
            Q0=qCreatedBy(id+"F22.planeOp",FACE);
            var sketch = newSketch(context, id + "F23", { "sketchPlane" : qUnion([Q0])});
            skCircle(sketch, "E59", {"center": v(10.4, 1.8) * mm, "radius": 0.2 * mm});
            skSolve(sketch);
        }
        {
            var Q0;
            Q0=makeQuery(id+"F23.imprint","IMPRINT",FACE,{"disambiguationData":[TD([[makeQuery(id+"F23.imprint","IMPRINT",EDGE,{"derivedFrom":sQuery(id+"F23.wireOp",EDGE,"E59")}),1.0]])]});
            var Q1;
            Q1=sQuery(id+"F21.wireOp",EDGE,"E48.left");
            var Q2;
            Q2=sQuery(id+"F21.wireOp",EDGE,"E52");
            var Q3;
            Q3=sQuery(id+"F21.wireOp",EDGE,"E50");
            var Q4;
            Q4=sQuery(id+"F21.wireOp",EDGE,"E53");
            var Q5;
            Q5=sQuery(id+"F21.wireOp",EDGE,"E56.1.0.0");
            var Q6;
            Q6=sQuery(id+"F21.wireOp",EDGE,"E56.1.0.1");
            var Q7;
            Q7=sQuery(id+"F21.wireOp",EDGE,"E56.1.0.2");
            var Q8;
            Q8=sQuery(id+"F21.wireOp",EDGE,"E56.1.0.3");
            var Q9;
            Q9=sQuery(id+"F21.wireOp",EDGE,"E56.1.0.4");
            var Q10;
            Q10=sQuery(id+"F21.wireOp",EDGE,"E56.2.0.1");
            var Q11;
            Q11=sQuery(id+"F21.wireOp",EDGE,"E56.2.0.2");
            var Q12;
            Q12=sQuery(id+"F21.wireOp",EDGE,"E56.3.0.0");
            var Q13;
            Q13=sQuery(id+"F21.wireOp",EDGE,"E56.2.0.3");
            var Q14;
            Q14=sQuery(id+"F21.wireOp",EDGE,"E56.3.0.1");
            var Q15;
            Q15=sQuery(id+"F21.wireOp",EDGE,"E56.3.0.2");
            var Q16;
            Q16=sQuery(id+"F21.wireOp",EDGE,"E56.4.0.1");
            var Q17;
            Q17=sQuery(id+"F21.wireOp",EDGE,"E56.3.0.4");
            var Q18;
            Q18=sQuery(id+"F21.wireOp",EDGE,"E56.4.0.2");
            var Q19;
            Q19=sQuery(id+"F21.wireOp",EDGE,"E56.3.0.3");
            var Q20;
            Q20=sQuery(id+"F21.wireOp",EDGE,"E56.4.0.3");
            var Q21;
            Q21=sQuery(id+"F21.wireOp",EDGE,"E56.5.0.0");
            var Q22;
            Q22=sQuery(id+"F21.wireOp",EDGE,"E56.5.0.1");
            var Q23;
            Q23=sQuery(id+"F21.wireOp",EDGE,"E56.5.0.2");
            var Q24;
            Q24=sQuery(id+"F21.wireOp",EDGE,"E56.5.0.3");
            var Q25;
            Q25=sQuery(id+"F21.wireOp",EDGE,"E56.5.0.4");
            var Q26;
            Q26=sQuery(id+"F21.wireOp",EDGE,"E57");
            var Q27;
            Q27=sQuery(id+"F21.wireOp",EDGE,"E58");
            sweep(context, id + "F24", {"operationType" : NewBodyOperationType.ADD, "profiles" : qUnion([Q0]), "path" : qUnion([Q1, Q2, Q3, Q4, Q5, Q6, Q7, Q8, Q9, Q10, Q11, Q12, Q13, Q14, Q15, Q16, Q17, Q18, Q19, Q20, Q21, Q22, Q23, Q24, Q25, Q26, Q27])});
        }
        {
            var Q0;
            Q0=qCreatedBy(id+"F20.planeOp",FACE);
            cPlane(context, id + "F25", {"entities" : qUnion([Q0]), "cplaneType" : CPlaneType.OFFSET, "offset" : 0.4 * mm, "width" : 150 * mm, "height" : 150 * mm});
        }
        {
            var Q0;
            Q0=qCreatedBy(id+"F25.planeOp",FACE);
            var sketch = newSketch(context, id + "F26", { "sketchPlane" : qUnion([Q0])});
            skLineSegment(sketch, "E60.bottom", {"start": v(10.4, -10.4) * mm, "end": v(10.4, 10.4) * mm});
            skLineSegment(sketch, "E60.top", {"start": v(-10.4, -10.4) * mm, "end": v(-10.4, 10.4) * mm});
            skLineSegment(sketch, "E60.left", {"start": v(9.6, -10.4) * mm, "end": v(-10.4, -10.4) * mm});
            skLineSegment(sketch, "E60.right", {"start": v(10.4, 10.4) * mm, "end": v(-10.4, 10.4) * mm});
            skPoint(sketch, "E60.middle", {"position": v(0, 0) * mm});
            skLineSegment(sketch, "E61", {"start": v(10.4, -7.2) * mm, "end": v(-9.6, -7.2) * mm});
            skLineSegment(sketch, "E62", {"start": v(-9.6, -8.8) * mm, "end": v(9.6, -8.8) * mm});
            skLineSegment(sketch, "E63", {"start": v(10.4, -10.4) * mm, "end": v(-10.4, -10.4) * mm});
            skArc(sketch, "E64", {"start": v(9.6, -8.8) * mm, "mid": v(10.4, -9.6) * mm, "end": v(9.6, -10.4) * mm});
            skArc(sketch, "E65", {"start": v(-9.6, -8.8) * mm, "mid": v(-10.4, -8) * mm, "end": v(-9.6, -7.2) * mm});
            skLineSegment(sketch, "E66", {"start": v(-9.6, -7.2) * mm, "end": v(9.6, -7.2) * mm});
            skLineSegment(sketch, "E67", {"start": v(9.6, -10.4) * mm, "end": v(-9.6, -10.4) * mm});
            skLineSegment(sketch, "E68.1.0.0", {"start": v(9.6, -7.2) * mm, "end": v(-9.6, -7.2) * mm});
            skArc(sketch, "E68.1.0.1", {"start": v(9.6, -5.6) * mm, "mid": v(10.4, -6.4) * mm, "end": v(9.6, -7.2) * mm});
            skLineSegment(sketch, "E68.1.0.2", {"start": v(-9.6, -5.6) * mm, "end": v(9.6, -5.6) * mm});
            skArc(sketch, "E68.1.0.3", {"start": v(-9.6, -5.6) * mm, "mid": v(-10.4, -4.8) * mm, "end": v(-9.6, -4) * mm});
            skLineSegment(sketch, "E68.1.0.4", {"start": v(-9.6, -4) * mm, "end": v(9.6, -4) * mm});
            skLineSegment(sketch, "E68.2.0.0", {"start": v(9.6, -4) * mm, "end": v(-9.6, -4) * mm});
            skArc(sketch, "E68.2.0.1", {"start": v(9.6, -2.4) * mm, "mid": v(10.4, -3.2) * mm, "end": v(9.6, -4) * mm});
            skLineSegment(sketch, "E68.2.0.2", {"start": v(-9.6, -2.4) * mm, "end": v(9.6, -2.4) * mm});
            skArc(sketch, "E68.2.0.3", {"start": v(-9.6, -2.4) * mm, "mid": v(-10.4, -1.6) * mm, "end": v(-9.6, -0.8) * mm});
            skLineSegment(sketch, "E68.2.0.4", {"start": v(-9.6, -0.8) * mm, "end": v(9.6, -0.8) * mm});
            skLineSegment(sketch, "E68.3.0.0", {"start": v(9.6, -0.8) * mm, "end": v(-9.6, -0.8) * mm});
            skArc(sketch, "E68.3.0.1", {"start": v(9.6, 0.8) * mm, "mid": v(10.4, 0) * mm, "end": v(9.6, -0.8) * mm});
            skLineSegment(sketch, "E68.3.0.2", {"start": v(-9.6, 0.8) * mm, "end": v(9.6, 0.8) * mm});
            skArc(sketch, "E68.3.0.3", {"start": v(-9.6, 0.8) * mm, "mid": v(-10.4, 1.6) * mm, "end": v(-9.6, 2.4) * mm});
            skLineSegment(sketch, "E68.3.0.4", {"start": v(-9.6, 2.4) * mm, "end": v(9.6, 2.4) * mm});
            skLineSegment(sketch, "E68.4.0.0", {"start": v(9.6, 2.4) * mm, "end": v(-9.6, 2.4) * mm});
            skArc(sketch, "E68.4.0.1", {"start": v(9.6, 4) * mm, "mid": v(10.4, 3.2) * mm, "end": v(9.6, 2.4) * mm});
            skLineSegment(sketch, "E68.4.0.2", {"start": v(-9.6, 4) * mm, "end": v(9.6, 4) * mm});
            skArc(sketch, "E68.4.0.3", {"start": v(-9.6, 4) * mm, "mid": v(-10.4, 4.8) * mm, "end": v(-9.6, 5.6) * mm});
            skLineSegment(sketch, "E68.4.0.4", {"start": v(-9.6, 5.6) * mm, "end": v(9.6, 5.6) * mm});
            skLineSegment(sketch, "E68.5.0.0", {"start": v(9.6, 5.6) * mm, "end": v(-9.6, 5.6) * mm});
            skArc(sketch, "E68.5.0.1", {"start": v(9.6, 7.2) * mm, "mid": v(10.4, 6.4) * mm, "end": v(9.6, 5.6) * mm});
            skLineSegment(sketch, "E68.5.0.2", {"start": v(-9.6, 7.2) * mm, "end": v(9.6, 7.2) * mm});
            skArc(sketch, "E68.5.0.3", {"start": v(-9.6, 7.2) * mm, "mid": v(-10.4, 8) * mm, "end": v(-9.6, 8.8) * mm});
            skLineSegment(sketch, "E68.5.0.4", {"start": v(-9.6, 8.8) * mm, "end": v(9.6, 8.8) * mm});
            skLineSegment(sketch, "E68.direction1", {"start": v(-9.6, -7.2) * mm, "end": v(-9.6, -4) * mm, "construction": true});
            skArc(sketch, "E69", {"start": v(9.6, 8.8) * mm, "mid": v(10.4, 9.6) * mm, "end": v(9.6, 10.4) * mm});
            skLineSegment(sketch, "E70", {"start": v(9.6, 10.4) * mm, "end": v(-10.4, 10.4) * mm});
            skSolve(sketch);
        }
        {
            var Q0;
            Q0=sQuery(id+"F26.wireOp",EDGE,"E63");
            var Q1;
            Q1=sQuery(id+"F26.wireOp",VERTEX,"E60.left.end");
            cPlane(context, id + "F27", {"entities" : qUnion([Q0, Q1]), "cplaneType" : CPlaneType.LINE_POINT, "offset" : 25 * mm, "width" : 150 * mm, "height" : 150 * mm});
        }
        {
            var Q0;
            Q0=qCreatedBy(id+"F27.planeOp",FACE);
            var sketch = newSketch(context, id + "F28", { "sketchPlane" : qUnion([Q0])});
            skCircle(sketch, "E71", {"center": v(10.4, 2.2) * mm, "radius": 0.2 * mm});
            skSolve(sketch);
        }
        {
            var Q0;
            Q0=makeQuery(id+"F28.imprint","IMPRINT",FACE,{"disambiguationData":[TD([[makeQuery(id+"F28.imprint","IMPRINT",EDGE,{"derivedFrom":sQuery(id+"F28.wireOp",EDGE,"E71")}),1.0]])]});
            var Q1;
            Q1=sQuery(id+"F26.wireOp",EDGE,"E60.left");
            var Q2;
            Q2=sQuery(id+"F26.wireOp",EDGE,"E64");
            var Q3;
            Q3=sQuery(id+"F26.wireOp",EDGE,"E62");
            var Q4;
            Q4=sQuery(id+"F26.wireOp",EDGE,"E65");
            var Q5;
            Q5=sQuery(id+"F26.wireOp",EDGE,"E68.1.0.0");
            var Q6;
            Q6=sQuery(id+"F26.wireOp",EDGE,"E68.1.0.1");
            var Q7;
            Q7=sQuery(id+"F26.wireOp",EDGE,"E68.1.0.2");
            var Q8;
            Q8=sQuery(id+"F26.wireOp",EDGE,"E68.1.0.3");
            var Q9;
            Q9=sQuery(id+"F26.wireOp",EDGE,"E68.2.0.0");
            var Q10;
            Q10=sQuery(id+"F26.wireOp",EDGE,"E68.2.0.2");
            var Q11;
            Q11=sQuery(id+"F26.wireOp",EDGE,"E68.2.0.3");
            var Q12;
            Q12=sQuery(id+"F26.wireOp",EDGE,"E68.3.0.0");
            var Q13;
            Q13=sQuery(id+"F26.wireOp",EDGE,"E68.3.0.2");
            var Q14;
            Q14=sQuery(id+"F26.wireOp",EDGE,"E68.3.0.3");
            var Q15;
            Q15=sQuery(id+"F26.wireOp",EDGE,"E68.3.0.4");
            var Q16;
            Q16=sQuery(id+"F26.wireOp",EDGE,"E68.4.0.2");
            var Q17;
            Q17=sQuery(id+"F26.wireOp",EDGE,"E68.4.0.3");
            var Q18;
            Q18=sQuery(id+"F26.wireOp",EDGE,"E68.5.0.0");
            var Q19;
            Q19=sQuery(id+"F26.wireOp",EDGE,"E68.5.0.2");
            var Q20;
            Q20=sQuery(id+"F26.wireOp",EDGE,"E68.5.0.3");
            var Q21;
            Q21=sQuery(id+"F26.wireOp",EDGE,"E68.5.0.4");
            var Q22;
            Q22=sQuery(id+"F26.wireOp",EDGE,"E70");
            var Q23;
            Q23=sQuery(id+"F26.wireOp",EDGE,"E69");
            var Q24;
            Q24=sQuery(id+"F26.wireOp",EDGE,"E68.5.0.1");
            var Q25;
            Q25=sQuery(id+"F26.wireOp",EDGE,"E68.4.0.1");
            var Q26;
            Q26=sQuery(id+"F26.wireOp",EDGE,"E68.3.0.1");
            var Q27;
            Q27=sQuery(id+"F26.wireOp",EDGE,"E68.2.0.1");
            sweep(context, id + "F29", {"operationType" : NewBodyOperationType.ADD, "profiles" : qUnion([Q0]), "path" : qUnion([Q1, Q2, Q3, Q4, Q5, Q6, Q7, Q8, Q9, Q10, Q11, Q12, Q13, Q14, Q15, Q16, Q17, Q18, Q19, Q20, Q21, Q22, Q23, Q24, Q25, Q26, Q27])});
        }
        {
            var Q0;
            Q0=qCreatedBy(id+"F25.planeOp",FACE);
            cPlane(context, id + "F30", {"entities" : qUnion([Q0]), "cplaneType" : CPlaneType.OFFSET, "offset" : 0.4 * mm, "width" : 150 * mm, "height" : 150 * mm});
        }
        {
            var Q0;
            Q0=qCreatedBy(id+"F30.planeOp",FACE);
            var sketch = newSketch(context, id + "F31", { "sketchPlane" : qUnion([Q0])});
            skLineSegment(sketch, "E72.bottom", {"start": v(-10.4, -10.4) * mm, "end": v(10.4, -10.4) * mm});
            skLineSegment(sketch, "E72.top", {"start": v(-10.4, 10.4) * mm, "end": v(10.4, 10.4) * mm});
            skLineSegment(sketch, "E72.left", {"start": v(-10.4, -9.6) * mm, "end": v(-10.4, 10.4) * mm});
            skLineSegment(sketch, "E72.right", {"start": v(10.4, -10.4) * mm, "end": v(10.4, 10.4) * mm});
            skPoint(sketch, "E72.middle", {"position": v(0, 0) * mm});
            skLineSegment(sketch, "E73", {"start": v(-7.2, -10.4) * mm, "end": v(-7.2, 9.6) * mm});
            skLineSegment(sketch, "E74", {"start": v(-8.8, 9.6) * mm, "end": v(-8.8, -9.6) * mm});
            skLineSegment(sketch, "E75", {"start": v(-10.4, -10.4) * mm, "end": v(-10.4, 10.4) * mm});
            skArc(sketch, "E76", {"start": v(-8.8, -9.6) * mm, "mid": v(-9.6, -10.4) * mm, "end": v(-10.4, -9.6) * mm});
            skArc(sketch, "E77", {"start": v(-8.8, 9.6) * mm, "mid": v(-8, 10.4) * mm, "end": v(-7.2, 9.6) * mm});
            skLineSegment(sketch, "E78", {"start": v(-7.2, 9.6) * mm, "end": v(-7.2, -9.6) * mm});
            skLineSegment(sketch, "E79", {"start": v(-10.4, -9.6) * mm, "end": v(-10.4, 9.6) * mm});
            skLineSegment(sketch, "E80.1.0.0", {"start": v(-7.2, -9.6) * mm, "end": v(-7.2, 9.6) * mm});
            skArc(sketch, "E80.1.0.1", {"start": v(-5.6, -9.6) * mm, "mid": v(-6.4, -10.4) * mm, "end": v(-7.2, -9.6) * mm});
            skLineSegment(sketch, "E80.1.0.2", {"start": v(-5.6, 9.6) * mm, "end": v(-5.6, -9.6) * mm});
            skArc(sketch, "E80.1.0.3", {"start": v(-5.6, 9.6) * mm, "mid": v(-4.8, 10.4) * mm, "end": v(-4, 9.6) * mm});
            skLineSegment(sketch, "E80.1.0.4", {"start": v(-4, 9.6) * mm, "end": v(-4, -9.6) * mm});
            skLineSegment(sketch, "E80.2.0.0", {"start": v(-4, -9.6) * mm, "end": v(-4, 9.6) * mm});
            skArc(sketch, "E80.2.0.1", {"start": v(-2.4, -9.6) * mm, "mid": v(-3.2, -10.4) * mm, "end": v(-4, -9.6) * mm});
            skLineSegment(sketch, "E80.2.0.2", {"start": v(-2.4, 9.6) * mm, "end": v(-2.4, -9.6) * mm});
            skArc(sketch, "E80.2.0.3", {"start": v(-2.4, 9.6) * mm, "mid": v(-1.6, 10.4) * mm, "end": v(-0.8, 9.6) * mm});
            skLineSegment(sketch, "E80.2.0.4", {"start": v(-0.8, 9.6) * mm, "end": v(-0.8, -9.6) * mm});
            skLineSegment(sketch, "E80.3.0.0", {"start": v(-0.8, -9.6) * mm, "end": v(-0.8, 9.6) * mm});
            skArc(sketch, "E80.3.0.1", {"start": v(0.8, -9.6) * mm, "mid": v(0, -10.4) * mm, "end": v(-0.8, -9.6) * mm});
            skLineSegment(sketch, "E80.3.0.2", {"start": v(0.8, 9.6) * mm, "end": v(0.8, -9.6) * mm});
            skArc(sketch, "E80.3.0.3", {"start": v(0.8, 9.6) * mm, "mid": v(1.6, 10.4) * mm, "end": v(2.4, 9.6) * mm});
            skLineSegment(sketch, "E80.3.0.4", {"start": v(2.4, 9.6) * mm, "end": v(2.4, -9.6) * mm});
            skLineSegment(sketch, "E80.4.0.0", {"start": v(2.4, -9.6) * mm, "end": v(2.4, 9.6) * mm});
            skArc(sketch, "E80.4.0.1", {"start": v(4, -9.6) * mm, "mid": v(3.2, -10.4) * mm, "end": v(2.4, -9.6) * mm});
            skLineSegment(sketch, "E80.4.0.2", {"start": v(4, 9.6) * mm, "end": v(4, -9.6) * mm});
            skArc(sketch, "E80.4.0.3", {"start": v(4, 9.6) * mm, "mid": v(4.8, 10.4) * mm, "end": v(5.6, 9.6) * mm});
            skLineSegment(sketch, "E80.4.0.4", {"start": v(5.6, 9.6) * mm, "end": v(5.6, -9.6) * mm});
            skLineSegment(sketch, "E80.5.0.0", {"start": v(5.6, -9.6) * mm, "end": v(5.6, 9.6) * mm});
            skArc(sketch, "E80.5.0.1", {"start": v(7.2, -9.6) * mm, "mid": v(6.4, -10.4) * mm, "end": v(5.6, -9.6) * mm});
            skLineSegment(sketch, "E80.5.0.2", {"start": v(7.2, 9.6) * mm, "end": v(7.2, -9.6) * mm});
            skArc(sketch, "E80.5.0.3", {"start": v(7.2, 9.6) * mm, "mid": v(8, 10.4) * mm, "end": v(8.8, 9.6) * mm});
            skLineSegment(sketch, "E80.5.0.4", {"start": v(8.8, 9.6) * mm, "end": v(8.8, -9.6) * mm});
            skLineSegment(sketch, "E80.direction1", {"start": v(-7.2, 9.6) * mm, "end": v(-4, 9.6) * mm, "construction": true});
            skArc(sketch, "E81", {"start": v(8.8, -9.6) * mm, "mid": v(9.6, -10.4) * mm, "end": v(10.4, -9.6) * mm});
            skLineSegment(sketch, "E82", {"start": v(10.4, -9.6) * mm, "end": v(10.4, 10.4) * mm});
            skSolve(sketch);
        }
        {
            var Q0;
            Q0=sQuery(id+"F31.wireOp",EDGE,"E75");
            var Q1;
            Q1=sQuery(id+"F31.wireOp",VERTEX,"E72.left.end");
            cPlane(context, id + "F32", {"entities" : qUnion([Q0, Q1]), "cplaneType" : CPlaneType.LINE_POINT, "offset" : 25 * mm, "width" : 150 * mm, "height" : 150 * mm});
        }
        {
            var Q0;
            Q0=qCreatedBy(id+"F32.planeOp",FACE);
            var sketch = newSketch(context, id + "F33", { "sketchPlane" : qUnion([Q0])});
            skCircle(sketch, "E83", {"center": v(10.4, 2.6) * mm, "radius": 0.2 * mm});
            skSolve(sketch);
        }
        {
            var Q0;
            Q0=makeQuery(id+"F33.imprint","IMPRINT",FACE,{"disambiguationData":[TD([[makeQuery(id+"F33.imprint","IMPRINT",EDGE,{"derivedFrom":sQuery(id+"F33.wireOp",EDGE,"E83")}),1.0]])]});
            var Q1;
            Q1=sQuery(id+"F31.wireOp",EDGE,"E72.left");
            var Q2;
            Q2=sQuery(id+"F31.wireOp",EDGE,"E76");
            var Q3;
            Q3=sQuery(id+"F31.wireOp",EDGE,"E74");
            var Q4;
            Q4=sQuery(id+"F31.wireOp",EDGE,"E77");
            var Q5;
            Q5=sQuery(id+"F31.wireOp",EDGE,"E80.1.0.0");
            var Q6;
            Q6=sQuery(id+"F31.wireOp",EDGE,"E80.1.0.1");
            var Q7;
            Q7=sQuery(id+"F31.wireOp",EDGE,"E80.1.0.2");
            var Q8;
            Q8=sQuery(id+"F31.wireOp",EDGE,"E80.1.0.3");
            var Q9;
            Q9=sQuery(id+"F31.wireOp",EDGE,"E80.2.0.0");
            var Q10;
            Q10=sQuery(id+"F31.wireOp",EDGE,"E80.2.0.1");
            var Q11;
            Q11=sQuery(id+"F31.wireOp",EDGE,"E80.2.0.2");
            var Q12;
            Q12=sQuery(id+"F31.wireOp",EDGE,"E80.2.0.3");
            var Q13;
            Q13=sQuery(id+"F31.wireOp",EDGE,"E80.3.0.0");
            var Q14;
            Q14=sQuery(id+"F31.wireOp",EDGE,"E80.3.0.1");
            var Q15;
            Q15=sQuery(id+"F31.wireOp",EDGE,"E80.3.0.2");
            var Q16;
            Q16=sQuery(id+"F31.wireOp",EDGE,"E80.3.0.3");
            var Q17;
            Q17=sQuery(id+"F31.wireOp",EDGE,"E80.3.0.4");
            var Q18;
            Q18=sQuery(id+"F31.wireOp",EDGE,"E80.4.0.1");
            var Q19;
            Q19=sQuery(id+"F31.wireOp",EDGE,"E80.4.0.2");
            var Q20;
            Q20=sQuery(id+"F31.wireOp",EDGE,"E80.4.0.3");
            var Q21;
            Q21=sQuery(id+"F31.wireOp",EDGE,"E80.5.0.0");
            var Q22;
            Q22=sQuery(id+"F31.wireOp",EDGE,"E80.5.0.1");
            var Q23;
            Q23=sQuery(id+"F31.wireOp",EDGE,"E80.5.0.2");
            var Q24;
            Q24=sQuery(id+"F31.wireOp",EDGE,"E80.5.0.3");
            var Q25;
            Q25=sQuery(id+"F31.wireOp",EDGE,"E80.5.0.4");
            var Q26;
            Q26=sQuery(id+"F31.wireOp",EDGE,"E81");
            var Q27;
            Q27=sQuery(id+"F31.wireOp",EDGE,"E82");
            sweep(context, id + "F34", {"operationType" : NewBodyOperationType.ADD, "profiles" : qUnion([Q0]), "path" : qUnion([Q1, Q2, Q3, Q4, Q5, Q6, Q7, Q8, Q9, Q10, Q11, Q12, Q13, Q14, Q15, Q16, Q17, Q18, Q19, Q20, Q21, Q22, Q23, Q24, Q25, Q26, Q27])});
        }
        {
            var Q0;
            Q0=qCreatedBy(id+"F30.planeOp",FACE);
            cPlane(context, id + "F35", {"entities" : qUnion([Q0]), "cplaneType" : CPlaneType.OFFSET, "offset" : 0.4 * mm, "width" : 150 * mm, "height" : 150 * mm});
        }
        {
            var Q0;
            Q0=qCreatedBy(id+"F35.planeOp",FACE);
            var sketch = newSketch(context, id + "F36", { "sketchPlane" : qUnion([Q0])});
            skLineSegment(sketch, "E84.bottom", {"start": v(-10.4, 10.4) * mm, "end": v(-10.4, -10.4) * mm});
            skLineSegment(sketch, "E84.top", {"start": v(10.4, 10.4) * mm, "end": v(10.4, -10.4) * mm});
            skLineSegment(sketch, "E84.left", {"start": v(-9.6, 10.4) * mm, "end": v(10.4, 10.4) * mm});
            skLineSegment(sketch, "E84.right", {"start": v(-10.4, -10.4) * mm, "end": v(10.4, -10.4) * mm});
            skPoint(sketch, "E84.middle", {"position": v(0, 0) * mm});
            skLineSegment(sketch, "E85", {"start": v(-10.4, 7.2) * mm, "end": v(9.6, 7.2) * mm});
            skLineSegment(sketch, "E86", {"start": v(9.6, 8.8) * mm, "end": v(-9.6, 8.8) * mm});
            skLineSegment(sketch, "E87", {"start": v(-10.4, 10.4) * mm, "end": v(10.4, 10.4) * mm});
            skArc(sketch, "E88", {"start": v(-9.6, 8.8) * mm, "mid": v(-10.4, 9.6) * mm, "end": v(-9.6, 10.4) * mm});
            skArc(sketch, "E89", {"start": v(9.6, 8.8) * mm, "mid": v(10.4, 8) * mm, "end": v(9.6, 7.2) * mm});
            skLineSegment(sketch, "E90", {"start": v(9.6, 7.2) * mm, "end": v(-9.6, 7.2) * mm});
            skLineSegment(sketch, "E91", {"start": v(-9.6, 10.4) * mm, "end": v(9.6, 10.4) * mm});
            skLineSegment(sketch, "E92.1.0.0", {"start": v(-9.6, 7.2) * mm, "end": v(9.6, 7.2) * mm});
            skArc(sketch, "E92.1.0.1", {"start": v(-9.6, 5.6) * mm, "mid": v(-10.4, 6.4) * mm, "end": v(-9.6, 7.2) * mm});
            skLineSegment(sketch, "E92.1.0.2", {"start": v(9.6, 5.6) * mm, "end": v(-9.6, 5.6) * mm});
            skArc(sketch, "E92.1.0.3", {"start": v(9.6, 5.6) * mm, "mid": v(10.4, 4.8) * mm, "end": v(9.6, 4) * mm});
            skLineSegment(sketch, "E92.1.0.4", {"start": v(9.6, 4) * mm, "end": v(-9.6, 4) * mm});
            skLineSegment(sketch, "E92.2.0.0", {"start": v(-9.6, 4) * mm, "end": v(9.6, 4) * mm});
            skArc(sketch, "E92.2.0.1", {"start": v(-9.6, 2.4) * mm, "mid": v(-10.4, 3.2) * mm, "end": v(-9.6, 4) * mm});
            skLineSegment(sketch, "E92.2.0.2", {"start": v(9.6, 2.4) * mm, "end": v(-9.6, 2.4) * mm});
            skArc(sketch, "E92.2.0.3", {"start": v(9.6, 2.4) * mm, "mid": v(10.4, 1.6) * mm, "end": v(9.6, 0.8) * mm});
            skLineSegment(sketch, "E92.2.0.4", {"start": v(9.6, 0.8) * mm, "end": v(-9.6, 0.8) * mm});
            skLineSegment(sketch, "E92.3.0.0", {"start": v(-9.6, 0.8) * mm, "end": v(9.6, 0.8) * mm});
            skArc(sketch, "E92.3.0.1", {"start": v(-9.6, -0.8) * mm, "mid": v(-10.4, 0) * mm, "end": v(-9.6, 0.8) * mm});
            skLineSegment(sketch, "E92.3.0.2", {"start": v(9.6, -0.8) * mm, "end": v(-9.6, -0.8) * mm});
            skArc(sketch, "E92.3.0.3", {"start": v(9.6, -0.8) * mm, "mid": v(10.4, -1.6) * mm, "end": v(9.6, -2.4) * mm});
            skLineSegment(sketch, "E92.3.0.4", {"start": v(9.6, -2.4) * mm, "end": v(-9.6, -2.4) * mm});
            skLineSegment(sketch, "E92.4.0.0", {"start": v(-9.6, -2.4) * mm, "end": v(9.6, -2.4) * mm});
            skArc(sketch, "E92.4.0.1", {"start": v(-9.6, -4) * mm, "mid": v(-10.4, -3.2) * mm, "end": v(-9.6, -2.4) * mm});
            skLineSegment(sketch, "E92.4.0.2", {"start": v(9.6, -4) * mm, "end": v(-9.6, -4) * mm});
            skArc(sketch, "E92.4.0.3", {"start": v(9.6, -4) * mm, "mid": v(10.4, -4.8) * mm, "end": v(9.6, -5.6) * mm});
            skLineSegment(sketch, "E92.4.0.4", {"start": v(9.6, -5.6) * mm, "end": v(-9.6, -5.6) * mm});
            skLineSegment(sketch, "E92.5.0.0", {"start": v(-9.6, -5.6) * mm, "end": v(9.6, -5.6) * mm});
            skArc(sketch, "E92.5.0.1", {"start": v(-9.6, -7.2) * mm, "mid": v(-10.4, -6.4) * mm, "end": v(-9.6, -5.6) * mm});
            skLineSegment(sketch, "E92.5.0.2", {"start": v(9.6, -7.2) * mm, "end": v(-9.6, -7.2) * mm});
            skArc(sketch, "E92.5.0.3", {"start": v(9.6, -7.2) * mm, "mid": v(10.4, -8) * mm, "end": v(9.6, -8.8) * mm});
            skLineSegment(sketch, "E92.5.0.4", {"start": v(9.6, -8.8) * mm, "end": v(-9.6, -8.8) * mm});
            skLineSegment(sketch, "E92.direction1", {"start": v(9.6, 7.2) * mm, "end": v(9.6, 4) * mm, "construction": true});
            skArc(sketch, "E93", {"start": v(-9.6, -8.8) * mm, "mid": v(-10.4, -9.6) * mm, "end": v(-9.6, -10.4) * mm});
            skLineSegment(sketch, "E94", {"start": v(-9.6, -10.4) * mm, "end": v(10.4, -10.4) * mm});
            skSolve(sketch);
        }
        {
            var Q0;
            Q0=sQuery(id+"F36.wireOp",VERTEX,"E84.top.start");
            var Q1;
            Q1=sQuery(id+"F36.wireOp",EDGE,"E84.left");
            cPlane(context, id + "F37", {"entities" : qUnion([Q0, Q1]), "cplaneType" : CPlaneType.LINE_POINT, "offset" : 25 * mm, "width" : 150 * mm, "height" : 150 * mm});
        }
        {
            var Q0;
            Q0=qCreatedBy(id+"F37.planeOp",FACE);
            var sketch = newSketch(context, id + "F38", { "sketchPlane" : qUnion([Q0])});
            skCircle(sketch, "E95", {"center": v(10.4, 3) * mm, "radius": 0.2 * mm});
            skSolve(sketch);
        }
        {
            var Q0;
            Q0=makeQuery(id+"F38.imprint","IMPRINT",FACE,{"disambiguationData":[TD([[makeQuery(id+"F38.imprint","IMPRINT",EDGE,{"derivedFrom":sQuery(id+"F38.wireOp",EDGE,"E95")}),1.0]])]});
            var Q1;
            Q1=sQuery(id+"F36.wireOp",EDGE,"E84.left");
            var Q2;
            Q2=sQuery(id+"F36.wireOp",EDGE,"E88");
            var Q3;
            Q3=sQuery(id+"F36.wireOp",EDGE,"E86");
            var Q4;
            Q4=sQuery(id+"F36.wireOp",EDGE,"E89");
            var Q5;
            Q5=sQuery(id+"F36.wireOp",EDGE,"E90");
            var Q6;
            Q6=sQuery(id+"F36.wireOp",EDGE,"E92.1.0.1");
            var Q7;
            Q7=sQuery(id+"F36.wireOp",EDGE,"E92.1.0.2");
            var Q8;
            Q8=sQuery(id+"F36.wireOp",EDGE,"E92.1.0.3");
            var Q9;
            Q9=sQuery(id+"F36.wireOp",EDGE,"E92.1.0.4");
            var Q10;
            Q10=sQuery(id+"F36.wireOp",EDGE,"E92.2.0.1");
            var Q11;
            Q11=sQuery(id+"F36.wireOp",EDGE,"E92.2.0.2");
            var Q12;
            Q12=sQuery(id+"F36.wireOp",EDGE,"E92.2.0.3");
            var Q13;
            Q13=sQuery(id+"F36.wireOp",EDGE,"E92.3.0.0");
            var Q14;
            Q14=sQuery(id+"F36.wireOp",EDGE,"E92.3.0.1");
            var Q15;
            Q15=sQuery(id+"F36.wireOp",EDGE,"E92.3.0.2");
            var Q16;
            Q16=sQuery(id+"F36.wireOp",EDGE,"E92.3.0.3");
            var Q17;
            Q17=sQuery(id+"F36.wireOp",EDGE,"E92.3.0.4");
            var Q18;
            Q18=sQuery(id+"F36.wireOp",EDGE,"E92.4.0.1");
            var Q19;
            Q19=sQuery(id+"F36.wireOp",EDGE,"E92.4.0.2");
            var Q20;
            Q20=sQuery(id+"F36.wireOp",EDGE,"E92.4.0.3");
            var Q21;
            Q21=sQuery(id+"F36.wireOp",EDGE,"E92.4.0.4");
            var Q22;
            Q22=sQuery(id+"F36.wireOp",EDGE,"E92.5.0.1");
            var Q23;
            Q23=sQuery(id+"F36.wireOp",EDGE,"E92.5.0.2");
            var Q24;
            Q24=sQuery(id+"F36.wireOp",EDGE,"E92.5.0.3");
            var Q25;
            Q25=sQuery(id+"F36.wireOp",EDGE,"E92.5.0.4");
            var Q26;
            Q26=sQuery(id+"F36.wireOp",EDGE,"E93");
            var Q27;
            Q27=sQuery(id+"F36.wireOp",EDGE,"E94");
            sweep(context, id + "F39", {"operationType" : NewBodyOperationType.ADD, "profiles" : qUnion([Q0]), "path" : qUnion([Q1, Q2, Q3, Q4, Q5, Q6, Q7, Q8, Q9, Q10, Q11, Q12, Q13, Q14, Q15, Q16, Q17, Q18, Q19, Q20, Q21, Q22, Q23, Q24, Q25, Q26, Q27])});
        }
    });
